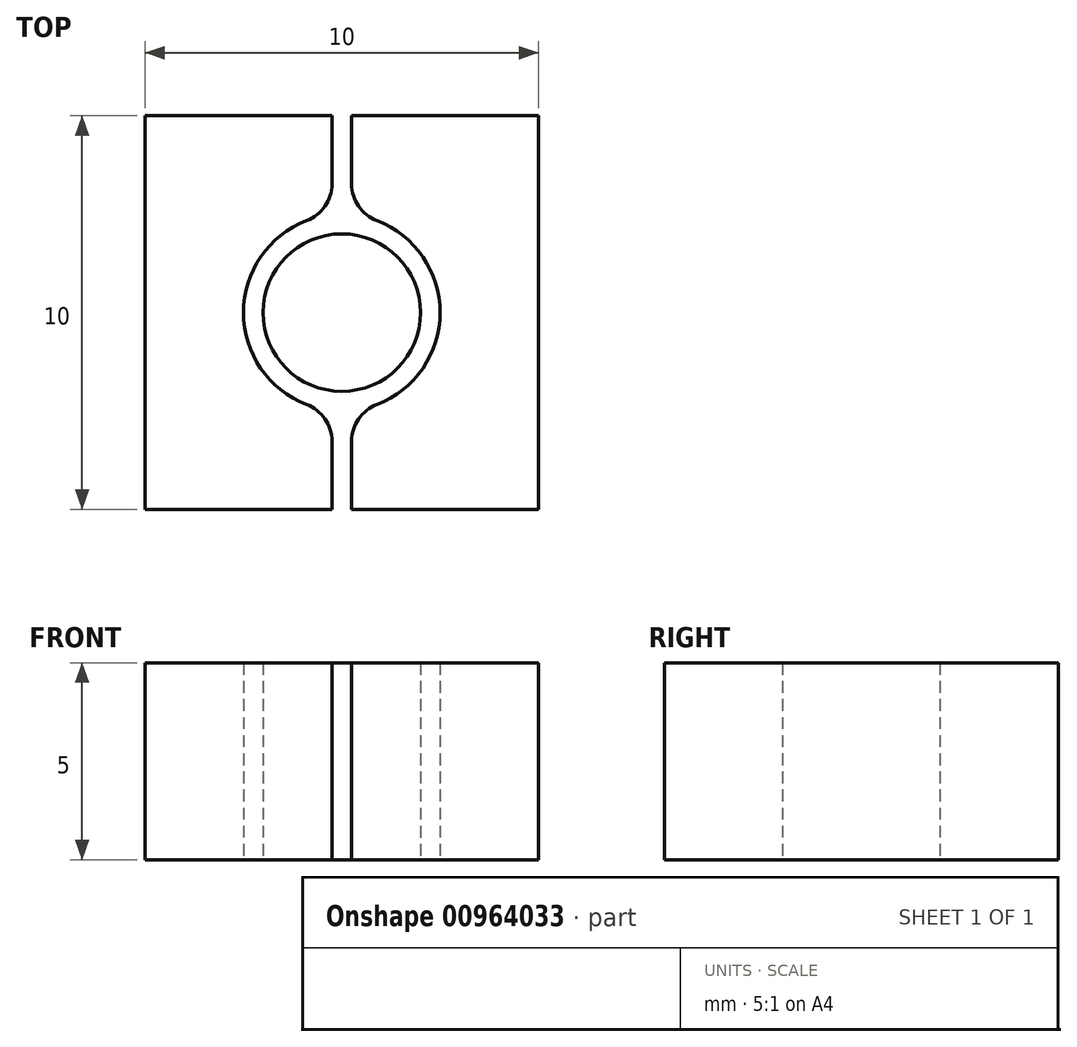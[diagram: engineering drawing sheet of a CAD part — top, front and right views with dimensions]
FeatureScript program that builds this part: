
annotation { "Feature Type Name" : "Feature", "Feature Type Description" : "" }
export const myFeature = defineFeature(function(context is Context, id is Id, definition is map)
    precondition{}
    {
        {
            var Q0;
            Q0=qCreatedBy(makeId("Top.planeOp"),FACE);
            var sketch = newSketch(context, id + "F0", { "sketchPlane" : qUnion([Q0])});
            skPoint(sketch, "E0", {"position": v(5, 5) * mm});
            skPoint(sketch, "E1", {"position": v(5, -5) * mm});
            skLineSegment(sketch, "E2", {"start": v(5, 5) * mm, "end": v(5, -5) * mm});
            skPoint(sketch, "E3", {"position": v(0.25, 5) * mm});
            skPoint(sketch, "E4", {"position": v(0.25, -5) * mm});
            skLineSegment(sketch, "E5", {"start": v(0.25, -5) * mm, "end": v(5, -5) * mm});
            skLineSegment(sketch, "E6", {"start": v(5, 5) * mm, "end": v(0.25, 5) * mm});
            skPoint(sketch, "E7", {"position": v(2.5, 0) * mm});
            skPoint(sketch, "E8", {"position": v(0, 2) * mm});
            skPoint(sketch, "E9", {"position": v(0, -2) * mm});
            skPoint(sketch, "E10", {"position": v(2, 0) * mm});
            skLineSegment(sketch, "E11.MirrorCS", {"start": v(-5, 5) * mm, "end": v(-5, -5) * mm});
            skLineSegment(sketch, "E12.MirrorCS", {"start": v(-5, 5) * mm, "end": v(-0.25, 5) * mm});
            skLineSegment(sketch, "E13.MirrorCS", {"start": v(-0.25, -5) * mm, "end": v(-5, -5) * mm});
            skArc(sketch, "E14", {"start": v(0, -2) * mm, "mid": v(2, 0) * mm, "end": v(0, 2) * mm});
            skLineSegment(sketch, "E15", {"start": v(0, 2) * mm, "end": v(0, -2) * mm});
            skArc(sketch, "E16.MirrorCS", {"start": v(0, -2) * mm, "mid": v(-2, 0) * mm, "end": v(0, 2) * mm});
            skArc(sketch, "E17", {"start": v(-0.25, 2.49) * mm, "mid": v(-2.5, 0) * mm, "end": v(-0.25, -2.49) * mm});
            skLineSegment(sketch, "E18", {"start": v(0.25, 5) * mm, "end": v(0.25, 2.49) * mm});
            skLineSegment(sketch, "E19", {"start": v(-0.25, 5) * mm, "end": v(-0.25, 2.49) * mm});
            skLineSegment(sketch, "E20", {"start": v(0.25, -5) * mm, "end": v(0.25, -2.49) * mm});
            skLineSegment(sketch, "E21", {"start": v(-0.25, -5) * mm, "end": v(-0.25, -2.49) * mm});
            skArc(sketch, "E22.trimOffspring", {"start": v(0.25, -2.49) * mm, "mid": v(2.5, 0) * mm, "end": v(0.25, 2.49) * mm});
            skSolve(sketch);
        }
        {
            var Q0;
            Q0=makeQuery(id+"F0.imprint","IMPRINT",FACE,{"disambiguationData":[TD([[makeQuery(id+"F0.imprint","IMPRINT",EDGE,{"derivedFrom":sQuery(id+"F0.wireOp",EDGE,"qpTuCAGg-9ZJZ-j3Cy-yi7a-v24poV9zIKmb")}),-1.0]])]});
            var Q1;
            Q1=makeQuery(id+"F0.imprint","IMPRINT",FACE,{"disambiguationData":[TD([[makeQuery(id+"F0.imprint","IMPRINT",EDGE,{"derivedFrom":sQuery(id+"F0.wireOp",EDGE,"4032d8c6-bab4-4f7d-a82e-da4e08cfaa6c0.MirrorCS")}),1.0]])]});
            var Q2;
            Q2=makeQuery(id+"F0.imprint","IMPRINT",FACE,{"disambiguationData":[TD([[makeQuery(id+"F0.imprint","IMPRINT",EDGE,{"derivedFrom":sQuery(id+"F0.wireOp",EDGE,"x3aBYImy-5CSo-Dzy0-CsFF-V8tosGpiXBP5")}),1.0]])]});
            var Q3;
            Q3=makeQuery(id+"F0.imprint","IMPRINT",FACE,{"disambiguationData":[TD([[makeQuery(id+"F0.imprint","IMPRINT",EDGE,{"derivedFrom":sQuery(id+"F0.wireOp",EDGE,"E2")}),-1.0]])]});
            var Q4;
            Q4=makeQuery(id+"F0.imprint","IMPRINT",FACE,{"disambiguationData":[TD([[makeQuery(id+"F0.imprint","IMPRINT",EDGE,{"derivedFrom":sQuery(id+"F0.wireOp",EDGE,"E11.MirrorCS")}),1.0]])]});
            var Q5;
            Q5=makeQuery(id+"F0.imprint","IMPRINT",FACE,{"disambiguationData":[TD([[makeQuery(id+"F0.imprint","IMPRINT",EDGE,{"derivedFrom":sQuery(id+"F0.wireOp",EDGE,"E15")}),-1.0]])]});
            var Q6;
            Q6=makeQuery(id+"F0.imprint","IMPRINT",FACE,{"disambiguationData":[TD([[makeQuery(id+"F0.imprint","IMPRINT",EDGE,{"derivedFrom":sQuery(id+"F0.wireOp",EDGE,"E14")}),1.0]])]});
            extrude(context, id + "F1", {"entities" : qUnion([Q0, Q1, Q2, Q3, Q4, Q5, Q6]), "depth" : 5 * mm, "offsetDistance" : 25 * mm});
        }
        {
            var Q0;
            Q0=makeQuery(id+"F1.opExtrude","SWEPT_EDGE",EDGE,{"disambiguationData":[OSD([sQuery(id+"F0.wireOp",EDGE,"E20"),sQuery(id+"F0.wireOp",EDGE,"E22.trimOffspring")])]});
            var Q1;
            Q1=makeQuery(id+"F1.opExtrude","SWEPT_EDGE",EDGE,{"disambiguationData":[OSD([sQuery(id+"F0.wireOp",EDGE,"E17"),sQuery(id+"F0.wireOp",EDGE,"E21")])]});
            var Q2;
            Q2=makeQuery(id+"F1.opExtrude","SWEPT_EDGE",EDGE,{"disambiguationData":[OSD([sQuery(id+"F0.wireOp",EDGE,"E18"),sQuery(id+"F0.wireOp",EDGE,"E22.trimOffspring")])]});
            var Q3;
            Q3=makeQuery(id+"F1.opExtrude","SWEPT_EDGE",EDGE,{"disambiguationData":[OSD([sQuery(id+"F0.wireOp",EDGE,"E17"),sQuery(id+"F0.wireOp",EDGE,"E19")])]});
            fillet(context, id + "F2", {"entities" : qUnion([Q0, Q1, Q2, Q3]), "radius" : 1 * mm, "tangentPropagation" : true, "allowEdgeOverflow" : false});
        }
    });
